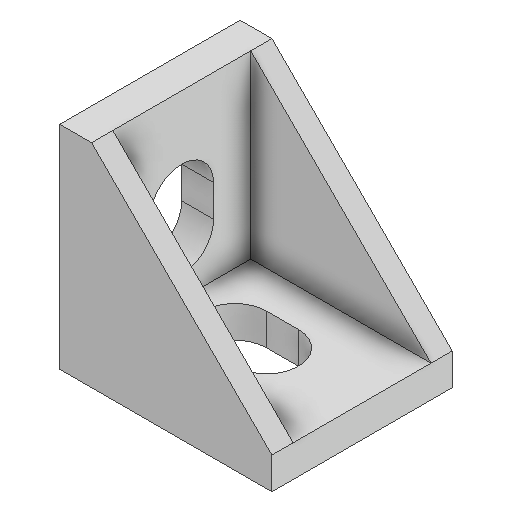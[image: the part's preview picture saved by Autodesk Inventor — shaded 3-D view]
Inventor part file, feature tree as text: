
AUTODESK INVENTOR PART (.ipt)
format: ipt  version: 2024.1 (Build 281209000, 209)  size: 131,584 bytes
history: native  units: in
note: dims shown in document units (in); Inventor stores cm internally (conversion verified against a paired STEP export)
features: other x3, sketch x2, plane x1
ambient origin geometry x8: Origin, YZ Plane, XZ Plane, XY Plane, X Axis, Y Axis, Z Axis, Center Point
bodies: Solid1 (feature_tree)
feature tree (6):
  other  "20x20 90 Gusset.ipt"
  other  "Solid1::20x20 90 Gusset.ipt"
  other  "TaggingFeature1"
  sketch  "Sketch3"  dims[d0=0.3937in]
  sketch  "Sketch4"
  plane  "Work Plane1"
